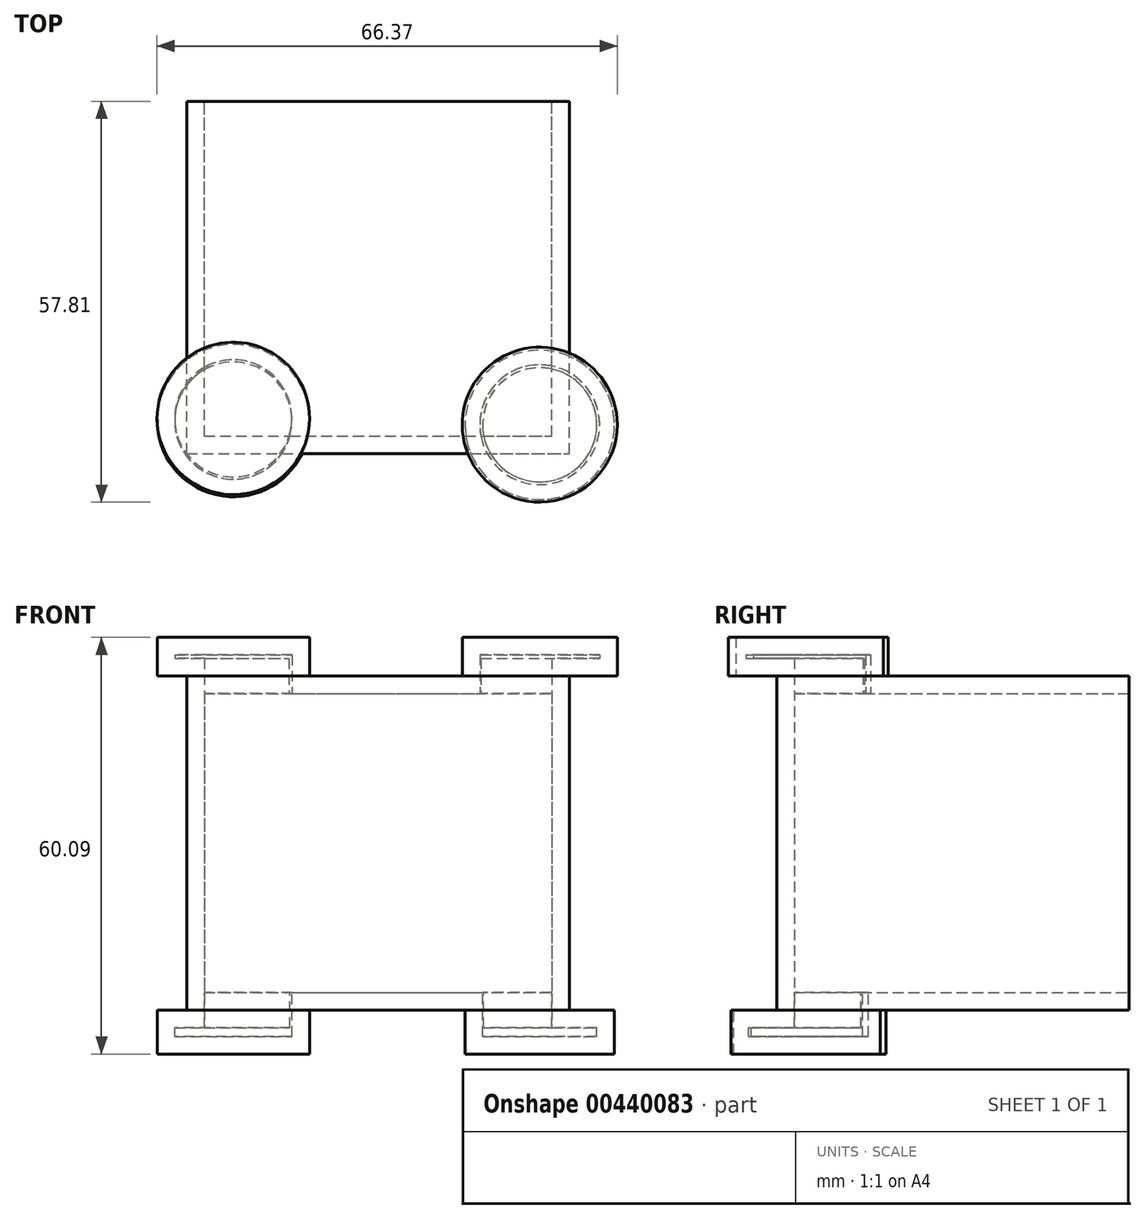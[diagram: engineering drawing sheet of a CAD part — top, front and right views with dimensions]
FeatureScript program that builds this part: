
annotation { "Feature Type Name" : "Feature", "Feature Type Description" : "" }
export const myFeature = defineFeature(function(context is Context, id is Id, definition is map)
    precondition{}
    {
        {
            var Q0;
            Q0=qCreatedBy(makeId("Front.planeOp"),FACE);
            var sketch = newSketch(context, id + "F0", { "sketchPlane" : qUnion([Q0])});
            skLineSegment(sketch, "E0.bottom", {"start": v(-25, 20.57) * mm, "end": v(30.18, 20.57) * mm});
            skLineSegment(sketch, "E0.top", {"start": v(-25, -27.58) * mm, "end": v(30.18, -27.58) * mm});
            skLineSegment(sketch, "E0.left", {"start": v(-25, 20.57) * mm, "end": v(-25, -27.58) * mm});
            skLineSegment(sketch, "E0.right", {"start": v(30.18, 20.57) * mm, "end": v(30.18, -27.58) * mm});
            skSolve(sketch);
        }
        {
            var Q0;
            Q0 = qSketchRegion(id + "F0", true);
            extrude(context, id + "F1", {"entities" : qUnion([Q0]), "depth" : 50.8 * mm});
        }
        {
            var Q0;
            Q0=makeQuery(id+"F1.opExtrude","SWEPT_FACE",FACE,{"disambiguationData":[OSD([sQuery(id+"F0.wireOp",EDGE,"E0.bottom")])]});
            var sketch = newSketch(context, id + "F2", { "sketchPlane" : qUnion([Q0])});
            skCircle(sketch, "E1", {"center": v(-18.29, -45.72) * mm, "radius": 10.99 * mm});
            skCircle(sketch, "E2", {"center": v(25.9, -46.63) * mm, "radius": 11.18 * mm});
            skSolve(sketch);
        }
        {
            var Q0;
            Q0=makeQuery(id+"F1.opExtrude","SWEPT_FACE",FACE,{"disambiguationData":[OSD([sQuery(id+"F0.wireOp",EDGE,"E0.top")])]});
            var sketch = newSketch(context, id + "F3", { "sketchPlane" : qUnion([Q0])});
            skCircle(sketch, "E3", {"center": v(-18.29, 46.05) * mm, "radius": 10.99 * mm});
            skCircle(sketch, "E4", {"center": v(25.9, 46.66) * mm, "radius": 10.77 * mm});
            skSolve(sketch);
        }
        {
            var Q0;
            Q0 = qSketchRegion(id + "F2", true);
            extrude(context, id + "F4", {"entities" : qUnion([Q0]), "operationType" : NewBodyOperationType.ADD, "depth" : 5.6 * mm});
        }
        {
            var Q0;
            Q0 = qSketchRegion(id + "F3", true);
            extrude(context, id + "F5", {"entities" : qUnion([Q0]), "operationType" : NewBodyOperationType.ADD, "depth" : 6.35 * mm});
        }
        {
            var Q0;
            Q0=makeQuery(id+"F1.opExtrude","CAP_FACE",FACE,{"disambiguationData":[OSD([sQuery(id+"F0.wireOp",EDGE,"E0.bottom"),sQuery(id+"F0.wireOp",EDGE,"E0.top"),sQuery(id+"F0.wireOp",EDGE,"E0.left"),sQuery(id+"F0.wireOp",EDGE,"E0.right")])],"isStart":true});
            shell(context, id + "F6", {"entities" : qUnion([Q0]), "thickness" : 2.54 * mm});
        }
    });
